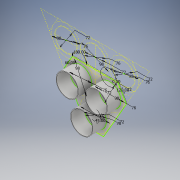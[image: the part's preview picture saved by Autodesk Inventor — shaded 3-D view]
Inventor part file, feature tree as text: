
AUTODESK INVENTOR PART (.ipt)
format: ipt  version: 2019 (Build 230136000, 136)  size: 188,928 bytes
history: native  units: in
note: dims shown in document units (in); Inventor stores cm internally (conversion verified against a paired STEP export)
features: extrude x3, sketch x2
ambient origin geometry x8: Origin, YZ Plane, XZ Plane, XY Plane, X Axis, Y Axis, Z Axis, Center Point
bodies: Solid1 (feature_tree)
feature tree (5):
  sketch  "Sketch1"  dims[d0=3.8583in d3=3.8583in]
  extrude  "Extrusion1"  Depth=3.8583in
  extrude  "Extrusion2"  Depth=3.8583in
  extrude  "Extrusion3"  Depth=3.8583in
  sketch  "Sketch2"  dims[d4=3.8583in d5=3.8583in d6=3.8583in d7=3.8583in d8=2.8346in d9=2.8346in d10=2.8346in d11=2.8346in d12=2.8346in d13=2.8346in d14=45.0deg d15=180.0deg d16=0.0in d17=2.9921in d18=2.9921in d19=2.9921in d20=2.9921in d21=2.9921in d22=2.9921in d23=60.0deg d24=120.0deg d25=1.7717in d26=0.0in d27=0.1181in d28=0.0in d29=0.2362in d30=0.4331in d31=0.2362in d32=0.4331in d33=0.2362in d34=0.4331in d35=0.1181in d36=0.0in]
